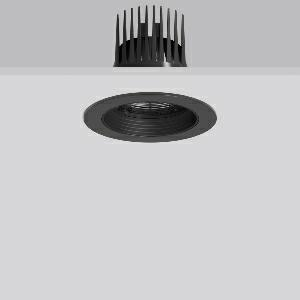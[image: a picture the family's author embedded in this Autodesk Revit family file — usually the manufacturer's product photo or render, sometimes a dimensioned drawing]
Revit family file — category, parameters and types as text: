
# Revit family: heledon_maxi_e_901768_003_1_76_dd94
name_source: partatom
category: Lighting Fixtures
units: mm (PartAtom-declared; Revit-internal decimal feet)

## family parameters
Cut with Voids When Loaded = No
Host = Face
Light Source = No
Part Type = Normal
Room Calculation Point = No
Round Connector Dimension = Use Diameter
Shared = No

## types (1)
- HELEDON maxi E (1 x LED Modul 940, 3750 lm, 4000)
    Apparent Load = 35 VA
    Approval mark = CE
    CIE Flux Codes = 96 100 100 100 100
    Color Rendering = 92
    Color Temperature = 4000
    Default Elevation = 1800 mm
    Description = Series: HELEDON maxi
Round recessed downlight. Housing: die-cast aluminium, powder-coated. Black plastic ring and recessed LED to prevent glare from the side. Optical assembly with lens made of plastic (polycarbonate) for the best homogeneous light distribution - can be changed without tools. Best colour rendering index Ra>90. Suitable for Recessed ceiling mounting. Installation without tools thanks to spring fastening system. Including separate LED converter with connecting cable 600 mm.High quality converter without flickering and stroboscopic effect. Through-wiring box (5 pole) available as accessory. The following accessories can be mounted without use of tools: interchangeable lenses, decorative glasses, honeycomb louvre, clear and frosted diffusers, white interchangeable plastic ring. 
Colour: deep black, matt (RAL 9005)
Diameter: 162 mm
Height: 3 mm
Cut-out diameter: 152 mm
Recess height: 200 mm
Luminaire: recess height: 135 mm
Lamp: LED
Socket: without socket
Colour temperature: 4000K
Colour rendering index (CRI): 92
System power: 35 W
Rated luminous flux: 3750 lm
Luminous efficiency: 107 lm/W
Control gear: Converter, dimmable, DALI
Protection class: II
Type of protection: IP 20
    Height = 0 mm  [stored 0 ft]
    Lamp = 1 x LED Modul 940
    Lamp Light Flux = 3750 lm
    Lamp count = 1
    Length = 162 mm
    Lifetime = 50000 h
    Luminous efficacy = 107 lm/W
    Manufacturer = RZB
    ModVariant = No
    Model = 901768.003.1.76
    Mounting Place = Ceiling
    Mounting Type = Recessed
    Number of Poles = 1
    OnlyDefault = Yes
    Power Factor = 1
    Product Name = HELEDON maxi E
    Product group = Recessed downlights
    ProductGroupID = 402
    Protection Class = Protection class II
    Protection Degree = IP 20
    RLX_Detail_Level = 1
    RLX_Emergency_Light_Flux = 0 lm
    RLX_Emergency_Type = 0
    RLX_Emergency_Type_DB = No
    RlxData = <blob elided: 122545 chars, md5=5c8ca9e9>
    Socket = socket
    Standby Power = 0 W
    System Light Flux = 3750 lm
    System Power = 35 W
    Type Comments = Product without accessories
    Type Image = 901663.003.jpg
    URL = http://relux.com
    VarID = ---
    Voltage = 230 V
    Voltage Range = 220-240 V
    Weight = 0.00 kg
    Width = 0 mm  [stored 0 ft]

note: [stored X ft] marks values corroborated as IEEE doubles in the binary element streams (Revit-internal decimal feet)

## geometry (parser evidence)
native form markers: Blend x4, Sweep x12
no freeform markers — native parametric forms only
